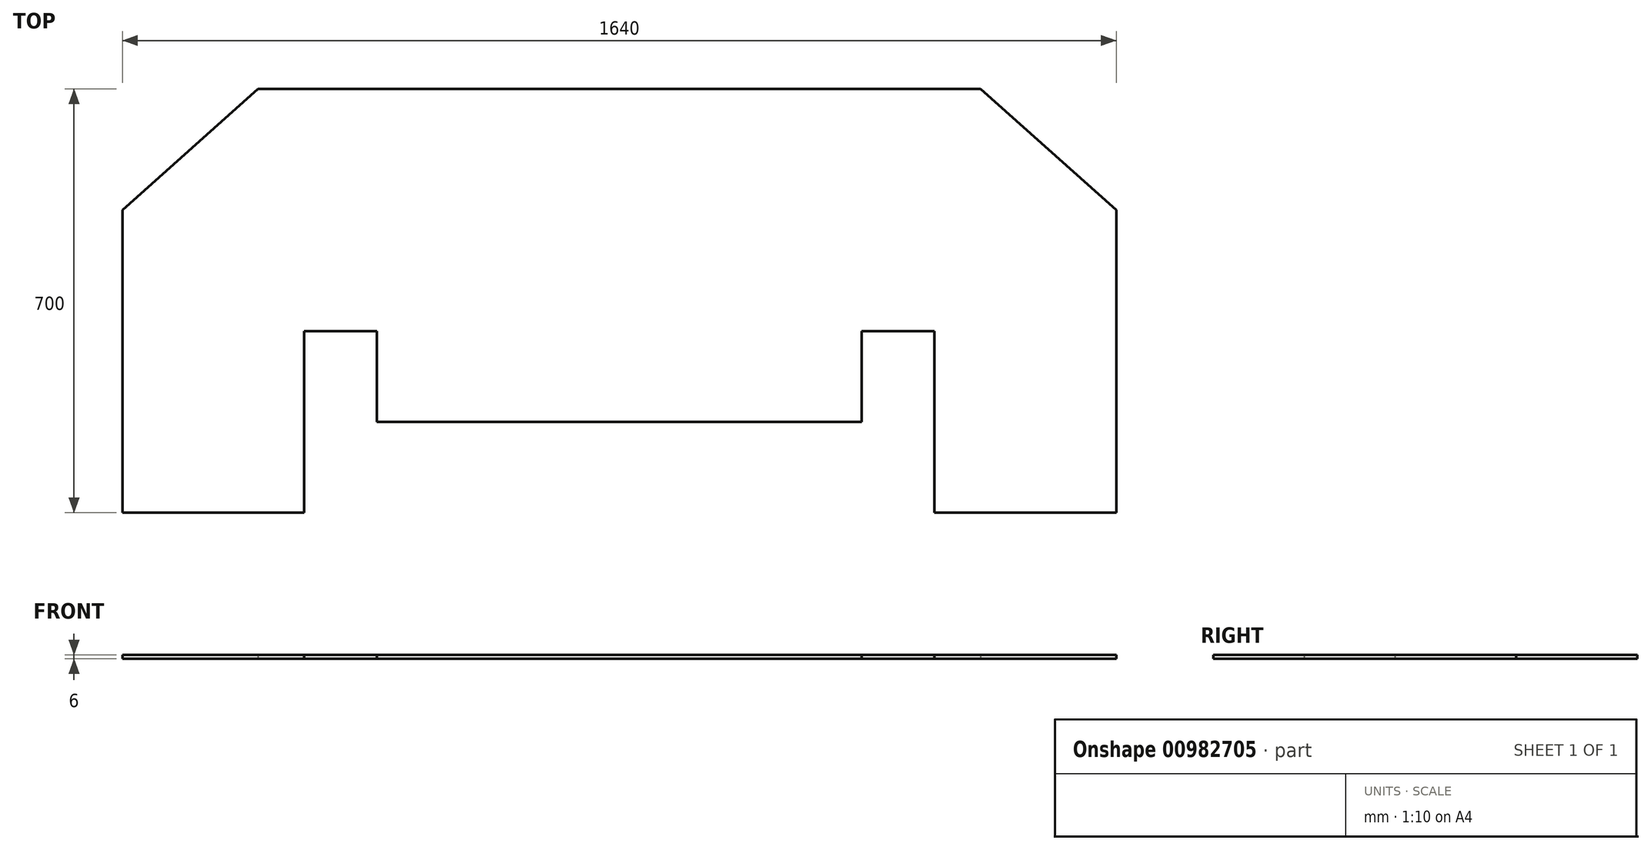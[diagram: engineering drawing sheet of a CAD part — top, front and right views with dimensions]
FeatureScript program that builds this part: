
annotation { "Feature Type Name" : "Feature", "Feature Type Description" : "" }
export const myFeature = defineFeature(function(context is Context, id is Id, definition is map)
    precondition{}
    {
        {
            var Q0;
            Q0=qCreatedBy(makeId("Top.planeOp"),FACE);
            var sketch = newSketch(context, id + "F0", { "sketchPlane" : qUnion([Q0])});
            skLineSegment(sketch, "E0", {"start": v(0, 0) * mm, "end": v(400, 0) * mm});
            skLineSegment(sketch, "E1", {"start": v(400, 0) * mm, "end": v(400, 150) * mm});
            skLineSegment(sketch, "E2", {"start": v(400, 150) * mm, "end": v(520, 150) * mm});
            skLineSegment(sketch, "E3", {"start": v(520, 150) * mm, "end": v(520, 0) * mm});
            skLineSegment(sketch, "E4", {"start": v(820, -150) * mm, "end": v(820, -29.43) * mm});
            skLineSegment(sketch, "E5", {"start": v(820, 350) * mm, "end": v(624.86, 524.54) * mm});
            skLineSegment(sketch, "E6", {"start": v(520, 0) * mm, "end": v(520, -150) * mm});
            skLineSegment(sketch, "E7", {"start": v(520, -150) * mm, "end": v(820, -150) * mm});
            skLineSegment(sketch, "E8", {"start": v(820, 350) * mm, "end": v(820, -29.43) * mm});
            skLineSegment(sketch, "E9", {"start": v(519.37, 550) * mm, "end": v(596.4, 550) * mm});
            skLineSegment(sketch, "E10", {"start": v(624.86, 524.54) * mm, "end": v(596.4, 550) * mm});
            skPoint(sketch, "E11.orphan", {"position": v(845.74, 350) * mm});
            skPoint(sketch, "E12.orphan", {"position": v(820, -295) * mm});
            skLineSegment(sketch, "E13.MirrorCS", {"start": v(0, 0) * mm, "end": v(-400, 0) * mm});
            skLineSegment(sketch, "E14.MirrorCS", {"start": v(-400, 0) * mm, "end": v(-400, 150) * mm});
            skLineSegment(sketch, "E15.MirrorCS", {"start": v(-400, 150) * mm, "end": v(-520, 150) * mm});
            skLineSegment(sketch, "E16.MirrorCS", {"start": v(-520, 150) * mm, "end": v(-520, 0) * mm});
            skLineSegment(sketch, "E17.MirrorCS", {"start": v(-520, 0) * mm, "end": v(-520, -150) * mm});
            skLineSegment(sketch, "E18.MirrorCS", {"start": v(-520, -150) * mm, "end": v(-820, -150) * mm});
            skLineSegment(sketch, "E19.MirrorCS", {"start": v(-820, -150) * mm, "end": v(-820, -29.43) * mm});
            skLineSegment(sketch, "E20.MirrorCS", {"start": v(-820, 350) * mm, "end": v(-820, -29.43) * mm});
            skLineSegment(sketch, "E21.MirrorCS", {"start": v(-820, 350) * mm, "end": v(-624.86, 524.54) * mm});
            skLineSegment(sketch, "E22.MirrorCS", {"start": v(-624.86, 524.54) * mm, "end": v(-596.4, 550) * mm});
            skLineSegment(sketch, "E23.MirrorCS", {"start": v(-519.37, 550) * mm, "end": v(-596.4, 550) * mm});
            skLineSegment(sketch, "E24", {"start": v(-519.37, 550) * mm, "end": v(519.37, 550) * mm});
            skSolve(sketch);
        }
        {
            var Q0;
            Q0 = qSketchRegion(id + "F0", true);
            extrude(context, id + "F1", {"entities" : qUnion([Q0]), "depth" : 6 * mm, "offsetDistance" : 25 * mm});
        }
    });
